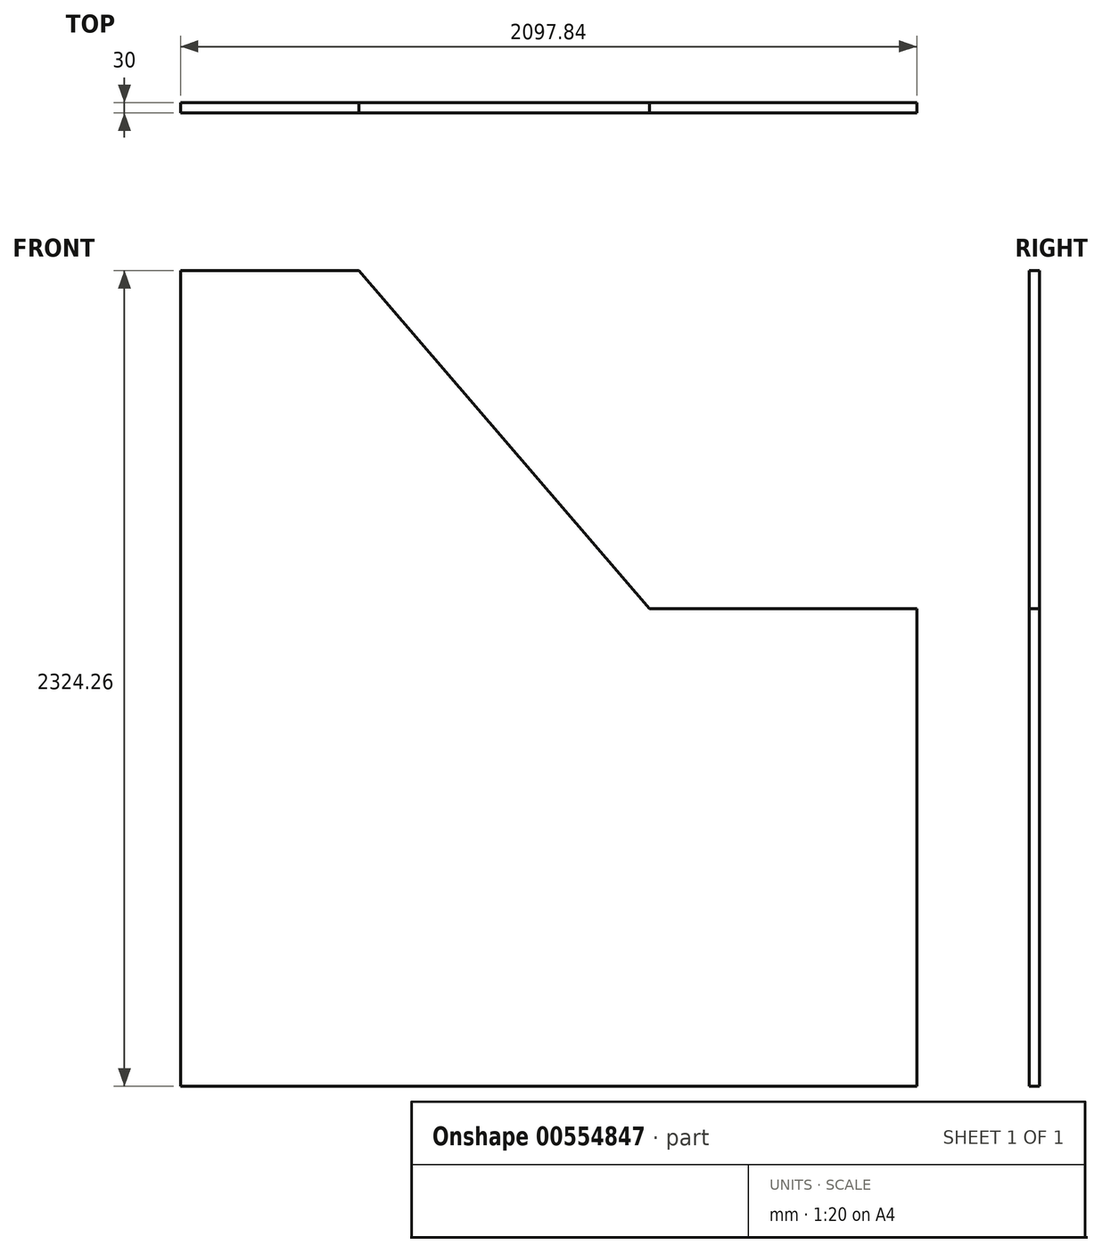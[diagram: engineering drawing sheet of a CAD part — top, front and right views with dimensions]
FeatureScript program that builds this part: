
annotation { "Feature Type Name" : "Feature", "Feature Type Description" : "" }
export const myFeature = defineFeature(function(context is Context, id is Id, definition is map)
    precondition{}
    {
        {
            var Q0;
            Q0=qCreatedBy(makeId("Front.planeOp"),FACE);
            var sketch = newSketch(context, id + "F0", { "sketchPlane" : qUnion([Q0])});
            skLineSegment(sketch, "E0", {"start": v(-1056.72, -1160.88) * mm, "end": v(1041.12, -1160.88) * mm});
            skLineSegment(sketch, "E1", {"start": v(1041.12, -1160.88) * mm, "end": v(1041.12, 200.23) * mm});
            skLineSegment(sketch, "E2", {"start": v(1041.12, 200.23) * mm, "end": v(279.07, 200.23) * mm});
            skLineSegment(sketch, "E3", {"start": v(279.07, 200.23) * mm, "end": v(-548.72, 1163.38) * mm});
            skLineSegment(sketch, "E4", {"start": v(-548.72, 1163.38) * mm, "end": v(-1056.72, 1163.38) * mm});
            skLineSegment(sketch, "E5", {"start": v(-1056.72, 1163.38) * mm, "end": v(-1056.72, -1160.88) * mm});
            skSolve(sketch);
        }
        {
            var Q0;
            Q0 = qSketchRegion(id + "F0", true);
            extrude(context, id + "F1", {"entities" : qUnion([Q0]), "depth" : 30 * mm, "offsetDistance" : 25.4 * mm});
        }
    });
